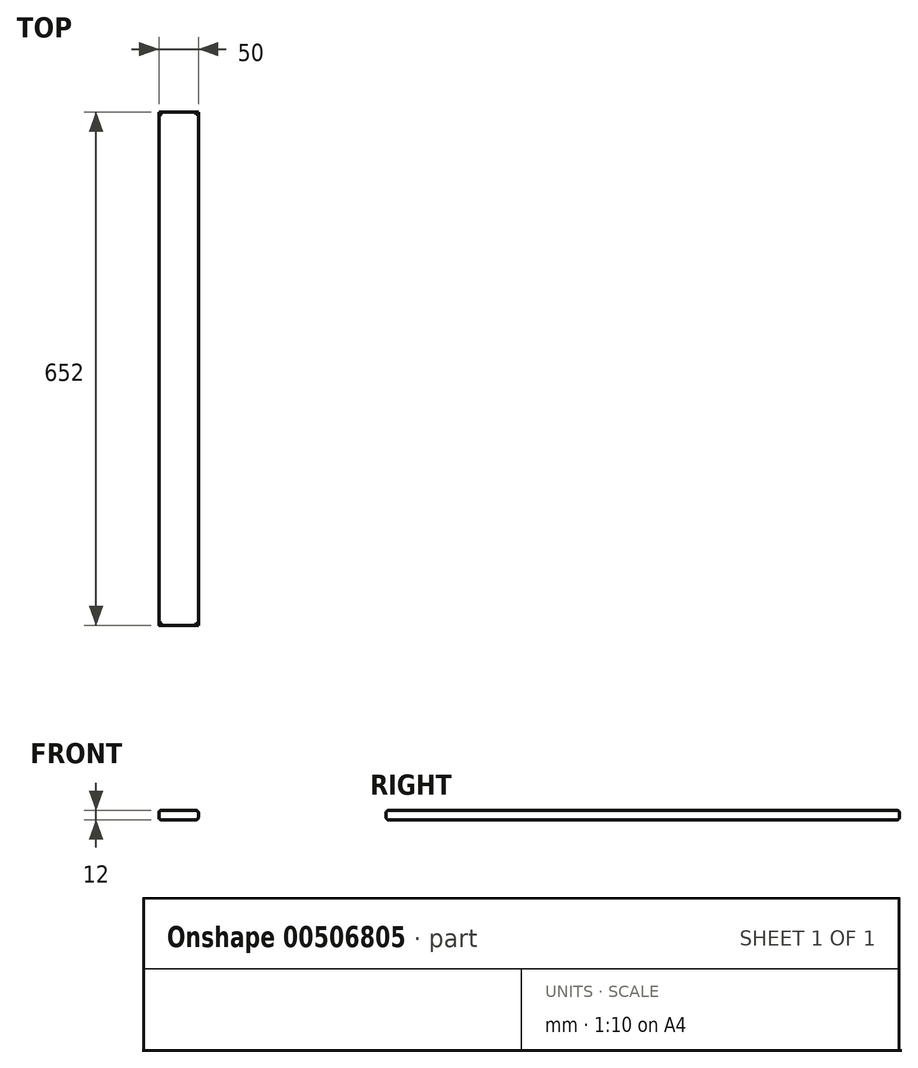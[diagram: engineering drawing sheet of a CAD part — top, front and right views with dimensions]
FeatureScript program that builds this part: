
annotation { "Feature Type Name" : "Feature", "Feature Type Description" : "" }
export const myFeature = defineFeature(function(context is Context, id is Id, definition is map)
    precondition{}
    {
        {
            var Q0;
            Q0=qCreatedBy(makeId("Front.planeOp"),FACE);
            var sketch = newSketch(context, id + "F0", { "sketchPlane" : qUnion([Q0])});
            skLineSegment(sketch, "E0.bottom", {"start": v(-117.08, 30.95) * mm, "end": v(-67.08, 30.95) * mm});
            skLineSegment(sketch, "E0.top", {"start": v(-117.08, 18.95) * mm, "end": v(-67.08, 18.95) * mm});
            skLineSegment(sketch, "E0.left", {"start": v(-117.08, 30.95) * mm, "end": v(-117.08, 18.95) * mm});
            skLineSegment(sketch, "E0.right", {"start": v(-67.08, 30.95) * mm, "end": v(-67.08, 18.95) * mm});
            skSolve(sketch);
        }
        {
            var Q0;
            Q0=makeQuery(id+"F0.imprint","IMPRINT",FACE,{"disambiguationData":[TD([[makeQuery(id+"F0.imprint","IMPRINT",EDGE,{"derivedFrom":sQuery(id+"F0.wireOp",EDGE,"E0.bottom")}),-1.0]])]});
            extrude(context, id + "F1", {"entities" : qUnion([Q0]), "depth" : 652 * mm});
        }
        {
            var Q0;
            Q0=makeQuery(id+"F1.opExtrude","SWEPT_FACE",FACE,{"disambiguationData":[OSD([sQuery(id+"F0.wireOp",EDGE,"E0.bottom")])]});
            var sketch = newSketch(context, id + "F2", { "sketchPlane" : qUnion([Q0])});
            skLineSegment(sketch, "E1", {"start": v(-67.08, -652) * mm, "end": v(-87.08, -652) * mm});
            skLineSegment(sketch, "E2", {"start": v(-87.08, -652) * mm, "end": v(-87.08, -352) * mm});
            skLineSegment(sketch, "E3", {"start": v(-87.08, -352) * mm, "end": v(-87.08, 0) * mm});
            skSolve(sketch);
        }
        {
            var Q0;
            Q0=makeQuery(id+"F1.opExtrude","SWEPT_FACE",FACE,{"disambiguationData":[OSD([sQuery(id+"F0.wireOp",EDGE,"E0.bottom")])]});
            var Q1;
            Q1=makeQuery(id+"F1.opExtrude","SWEPT_FACE",FACE,{"disambiguationData":[OSD([sQuery(id+"F0.wireOp",EDGE,"E0.top")])]});
            fillet(context, id + "F3", {"entities" : qUnion([Q0, Q1]), "radius" : 3 * mm, "tangentPropagation" : true, "allowEdgeOverflow" : false});
        }
    });
